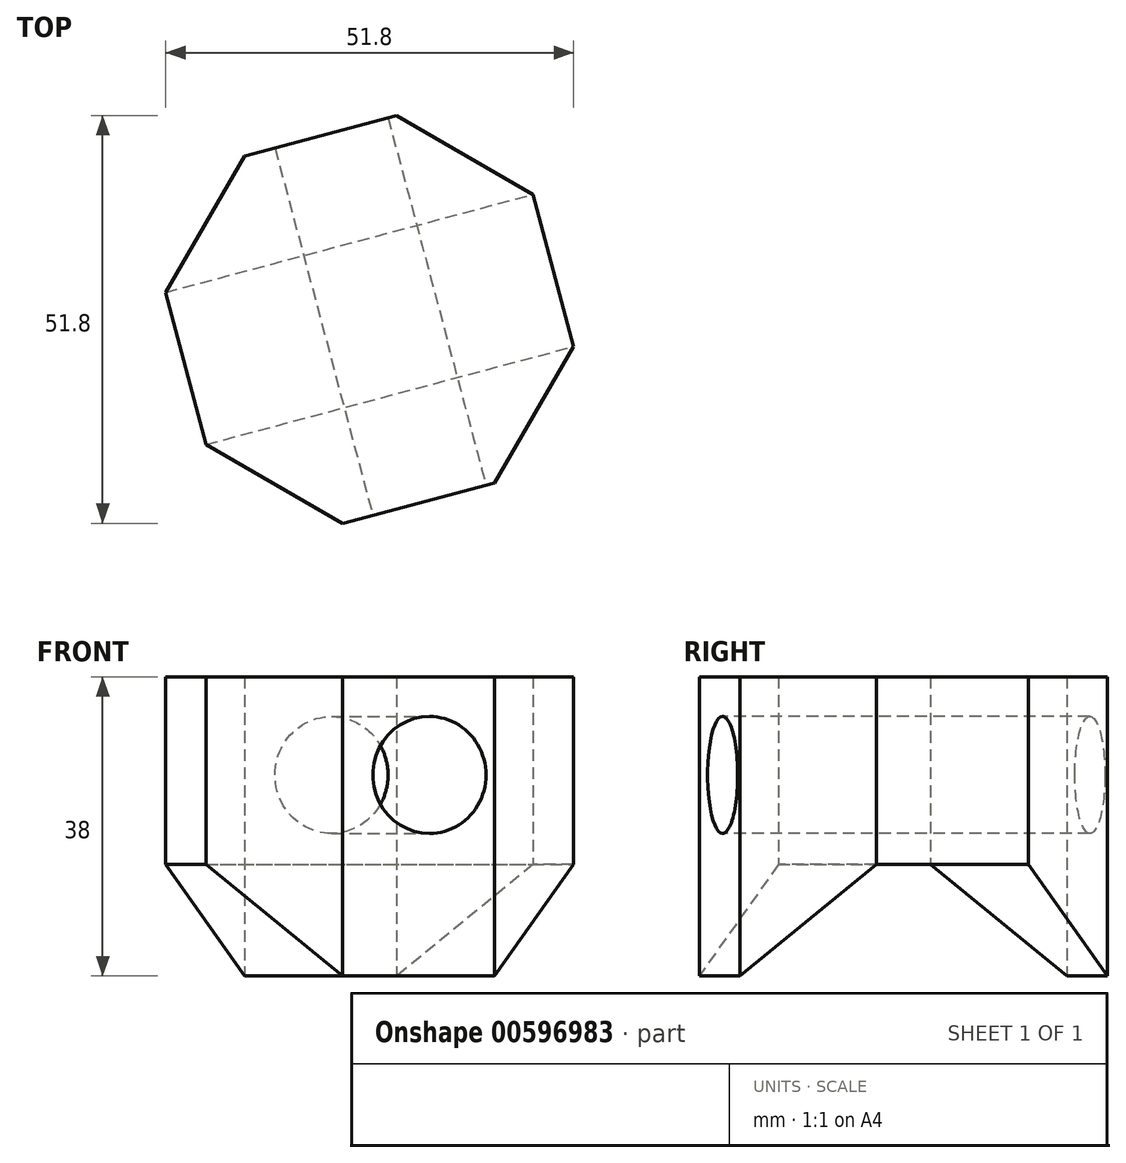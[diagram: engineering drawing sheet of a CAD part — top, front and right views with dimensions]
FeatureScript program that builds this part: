
annotation { "Feature Type Name" : "Feature", "Feature Type Description" : "" }
export const myFeature = defineFeature(function(context is Context, id is Id, definition is map)
    precondition{}
    {
        {
            var Q0;
            Q0=qCreatedBy(makeId("Top.planeOp"),FACE);
            var sketch = newSketch(context, id + "F0", { "sketchPlane" : qUnion([Q0])});
            skCircle(sketch, "E0.cCircle", {"center": v(0, 0) * mm, "radius": 24.14 * mm, "construction": true});
            skLineSegment(sketch, "E0.0", {"start": v(-25.9, 3.44) * mm, "end": v(-15.88, 20.75) * mm});
            skLineSegment(sketch, "E0.1", {"start": v(-15.88, 20.75) * mm, "end": v(3.44, 25.9) * mm});
            skLineSegment(sketch, "E0.2", {"start": v(3.44, 25.9) * mm, "end": v(20.75, 15.88) * mm});
            skLineSegment(sketch, "E0.3", {"start": v(20.75, 15.88) * mm, "end": v(25.9, -3.44) * mm});
            skLineSegment(sketch, "E0.4", {"start": v(25.9, -3.44) * mm, "end": v(15.88, -20.75) * mm});
            skLineSegment(sketch, "E0.5", {"start": v(15.88, -20.75) * mm, "end": v(-3.44, -25.9) * mm});
            skLineSegment(sketch, "E0.6", {"start": v(-3.44, -25.9) * mm, "end": v(-20.75, -15.88) * mm});
            skLineSegment(sketch, "E0.7", {"start": v(-20.75, -15.88) * mm, "end": v(-25.9, 3.44) * mm});
            skPoint(sketch, "E0.0.midPoint", {"position": v(-20.9, 12.1) * mm});
            skSolve(sketch);
        }
        {
            var Q0;
            Q0=makeQuery(id+"F0.imprint","IMPRINT",FACE,{"disambiguationData":[TD([[makeQuery(id+"F0.imprint","IMPRINT",EDGE,{"derivedFrom":sQuery(id+"F0.wireOp",EDGE,"E0.0")}),-1.0]])]});
            extrude(context, id + "F1", {"entities" : qUnion([Q0]), "depth" : 48 * mm, "offsetDistance" : 25.4 * mm});
        }
        {
            var Q0;
            Q0=makeQuery(id+"F1.opExtrude","SWEPT_FACE",FACE,{"disambiguationData":[OSD([sQuery(id+"F0.wireOp",EDGE,"E0.3")])]});
            var sketch = newSketch(context, id + "F2", { "sketchPlane" : qUnion([Q0])});
            skCircle(sketch, "E1.cCircle", {"center": v(0, 0) * mm, "radius": 24.14 * mm, "construction": true});
            skLineSegment(sketch, "E1.0", {"start": v(-24.14, 10) * mm, "end": v(-10, 24.14) * mm});
            skLineSegment(sketch, "E1.1", {"start": v(-10, 24.14) * mm, "end": v(10, 24.14) * mm});
            skLineSegment(sketch, "E1.2", {"start": v(10, 24.14) * mm, "end": v(24.14, 10) * mm});
            skLineSegment(sketch, "E1.3", {"start": v(24.14, 10) * mm, "end": v(24.14, -10) * mm});
            skLineSegment(sketch, "E1.4", {"start": v(24.14, -10) * mm, "end": v(10, -24.14) * mm});
            skLineSegment(sketch, "E1.5", {"start": v(10, -24.14) * mm, "end": v(-10, -24.14) * mm});
            skLineSegment(sketch, "E1.6", {"start": v(-10, -24.14) * mm, "end": v(-24.14, -10) * mm});
            skLineSegment(sketch, "E1.7", {"start": v(-24.14, -10) * mm, "end": v(-24.14, 10) * mm});
            skPoint(sketch, "E1.0.midPoint", {"position": v(-17.07, 17.07) * mm});
            skSolve(sketch);
        }
        {
            var Q0;
            {var subQ5=sQuery(id+"F2.wireOp",EDGE,"E1.0");Q0=makeQuery(id+"F2.imprint","IMPRINT",FACE,{"disambiguationData":[TD([[makeQuery(id+"F2.imprint","IMPRINT",EDGE,{"derivedFrom":subQ5}),-1.0]])]});}
            var Q1;
            {var subQ0=sQuery(id+"F2.wireOp",EDGE,"E1.1");Q1=makeQuery(id+"F2.imprint","IMPRINT",FACE,{"disambiguationData":[TD([[makeQuery(id+"F2.imprint","IMPRINT",EDGE,{"derivedFrom":subQ0}),-1.0]])]});}
            extrude(context, id + "F3", {"entities" : qUnion([Q0, Q1]), "operationType" : NewBodyOperationType.REMOVE, "endBound" : BoundingType.THROUGH_ALL, "oppositeDirection" : true, "depth" : 25.4 * mm, "offsetDistance" : 25.4 * mm});
        }
        {
            var Q0;
            Q0=makeQuery(id+"F1.opExtrude","SWEPT_FACE",FACE,{"disambiguationData":[OSD([sQuery(id+"F0.wireOp",EDGE,"E0.5")])]});
            var sketch = newSketch(context, id + "F4", { "sketchPlane" : qUnion([Q0])});
            skCircle(sketch, "E2", {"center": v(1.43, 35.53) * mm, "radius": 7.43 * mm});
            skSolve(sketch);
        }
        {
            var Q0;
            Q0=makeQuery(id+"F4.imprint","IMPRINT",FACE,{"disambiguationData":[TD([[makeQuery(id+"F4.imprint","IMPRINT",EDGE,{"derivedFrom":sQuery(id+"F4.wireOp",EDGE,"E2")}),1.0]])]});
            extrude(context, id + "F5", {"entities" : qUnion([Q0]), "operationType" : NewBodyOperationType.REMOVE, "endBound" : BoundingType.THROUGH_ALL, "oppositeDirection" : true, "depth" : 25.4 * mm, "offsetDistance" : 25.4 * mm});
        }
    });
